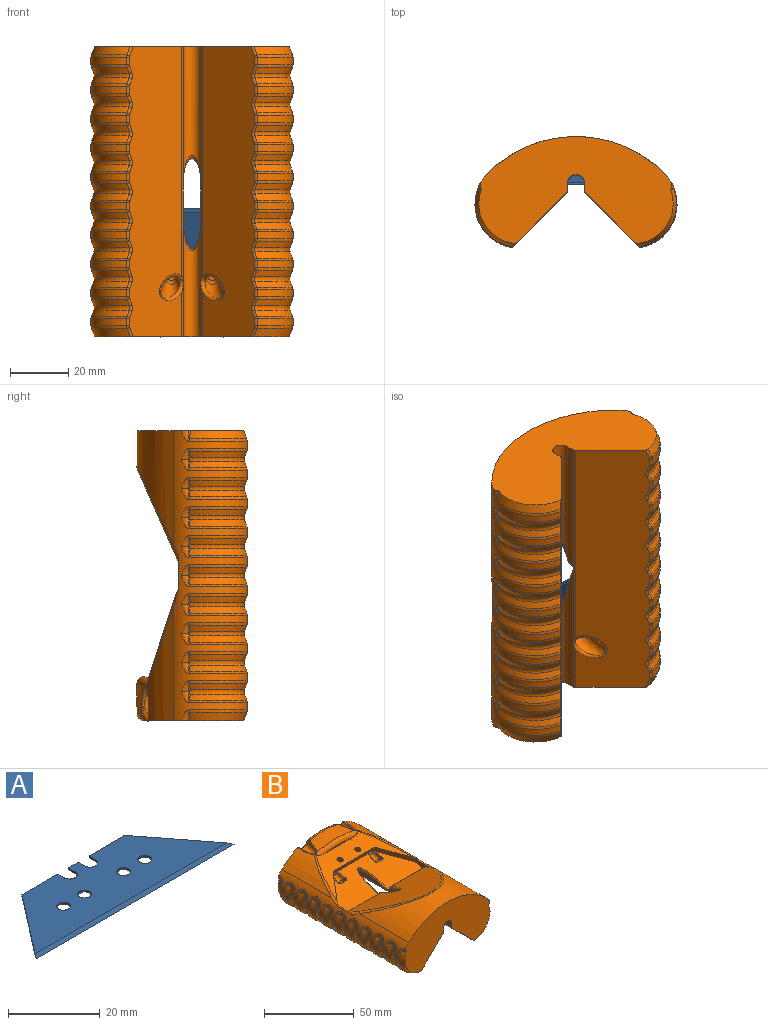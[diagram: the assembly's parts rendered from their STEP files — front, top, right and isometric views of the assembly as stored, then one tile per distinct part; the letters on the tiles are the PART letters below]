
ASSEMBLY  parts=2 mates=1
PART A: 19 faces, bbox 61x19x0.5 mm
  f0: plane 19x14.66mm, normal (-0.79,0.61,0), area 11.6mm2, adj f2,f3,f8,f17,f18
  f1: plane 19x14.66mm, normal (0.79,0.61,0), area 11.6mm2, adj f2,f3,f9,f17,f18
  f2: plane 59.02x17.71mm, normal (0,0,1), area 753.2mm2, adj f0,f1,f4,f5,f6,f7,f8,f9
  f3: plane 59.02x17.71mm, normal (0,0,-1), area 753.2mm2, adj f0,f1,f4,f5,f6,f7,f8,f9
  f4: plane 3.05x0.5mm, normal (0,1,0), area 1.5mm2, adj f2,f3,f5,f12
  f5: plane 2x0.5mm, normal (-1,0,0), area 1mm2, adj f2,f3,f4,f6
  f6: cylinder r=1.65mm len=3.3mm, axis (0,0,-1), area 2.6mm2, adj f2,f3,f5,f7
  f7: plane 2x0.5mm, normal (1,0,0), area 1mm2, adj f2,f3,f6,f8
  f8: plane 11.01x0.5mm, normal (0,1,0), area 5.5mm2, adj f0,f2,f3,f7
  f9: plane 11.01x0.5mm, normal (0,1,0), area 5.5mm2, adj f1,f2,f3,f10
  f10: plane 2x0.5mm, normal (-1,0,0), area 1mm2, adj f2,f3,f9,f11
  f11: cylinder r=1.65mm len=3.3mm, axis (0,0,-1), area 2.6mm2, adj f2,f3,f10,f12
  f12: plane 2x0.5mm, normal (1,0,0), area 1mm2, adj f2,f3,f4,f11
  f13: cylinder r=1.5mm len=3mm, axis (0,0,-1), area 4.7mm2, adj f2,f3
  f14: cylinder r=1.5mm len=3mm, axis (0,0,-1), area 4.7mm2, adj f2,f3
  f15: cylinder r=1.5mm len=3mm, axis (0,0,-1), area 4.7mm2, adj f2,f3
  f16: cylinder r=1.5mm len=3mm, axis (0,0,-1), area 4.7mm2, adj f2,f3
  f17: plane 61x1.29mm, normal (0,-0.19,0.98), area 78.6mm2, adj f0,f1,f2,f18
  f18: plane 61x1.29mm, normal (0,-0.19,-0.98), area 78.6mm2, adj f0,f1,f3,f17
PART B: 395 faces, bbox 78.7x113.5x44.1 mm
  f0: plane 47.73x2.33mm, normal (1,0,0), area 102.8mm2, adj f4,f19,f263,f394
  f1: plane 48.81x2.33mm, normal (-1,0,0), area 112.2mm2, adj f7,f17,f388,f389,f390,f393
  f2: cylinder r=43mm len=39.01mm, axis (0,1,0), area 409.2mm2, adj f4,f5,f94,f155
  f3: cylinder r=43mm len=30.05mm, axis (0,1,0), area 245.3mm2, adj f94,f95,f156,f159,f160,f246
  f4: plane 68.06x36.3mm, normal (0,1,0), area 1526.5mm2, adj f0,f2,f5,f6,f8,f9,f10,f16
  f5: cylinder r=15mm len=100mm, axis (0,1,0), area 1096.3mm2, adj f2,f4,f7,f13,f20,f51,f155,f203
  f6: plane 100x18.06mm, normal (0.71,0,-0.71), area 2413.3mm2, adj f4,f7,f266,f267,f268,f269,f270,f271
  f7: plane 67.06x36.92mm, normal (0,-1,0), area 1601.5mm2, adj f1,f5,f6,f8,f9,f15,f17,f20
  f8: cylinder r=15mm len=100mm, axis (0,1,0), area 1092.7mm2, adj f4,f7,f10,f14,f20,f52,f154,f163
  f9: plane 100x18.06mm, normal (-0.71,0,-0.71), area 2413.1mm2, adj f4,f7,f325,f326,f327,f328,f329,f330
  f10: cylinder r=43mm len=39.01mm, axis (0,1,0), area 409.2mm2, adj f4,f8,f95,f154
  f11: plane 32.7x3.41mm, normal (0,-0.95,-0.31), area 91.9mm2, adj f12,f13,f14,f25,f28,f31,f250,f255
  f12: plane 62x24.87mm, normal (0,-0.31,0.95), area 1116.5mm2, adj f11,f13,f14,f21,f22,f23,f24,f250
  f13: plane 20.34x15.87mm, normal (0.79,-0.58,-0.19), area 72.5mm2, adj f5,f11,f12,f21,f25,f51,f155,f255
  f14: plane 20.34x15.87mm, normal (-0.79,-0.58,-0.19), area 72.5mm2, adj f8,f11,f12,f22,f25,f52,f154,f257
  f15: plane 48.81x2.33mm, normal (1,0,0), area 112.2mm2, adj f7,f17,f384,f385,f386,f394
  f16: plane 47.73x2.33mm, normal (-1,0,0), area 102.8mm2, adj f4,f19,f265,f393
  f17: cylinder r=3mm len=46.59mm, axis (0,1,0), area 384.1mm2, adj f1,f7,f15,f387
  f18: plane 62x34.72mm, normal (0,0.41,0.91), area 1609.9mm2, adj f21,f22,f243,f244,f245,f247,f248,f386
  f19: cylinder r=3mm len=40.56mm, axis (0,1,0), area 316.9mm2, adj f0,f4,f16,f264
  f20: cylinder r=43mm len=60.81mm, axis (0,1,0), area 1458.6mm2, adj f5,f7,f8,f244
  f21: plane 10.53x3.88mm, normal (1,0,0), area 22.4mm2, adj f12,f13,f18,f24,f51,f245,f247
  f22: plane 10.53x3.88mm, normal (-1,0,0), area 22.4mm2, adj f12,f14,f18,f23,f52,f243,f248
  f23: plane 26.92x1.51mm, normal (0,0.95,0.31), area 42.8mm2, adj f12,f22,f248,f390
  f24: plane 26.92x1.51mm, normal (0,0.95,0.31), area 42.8mm2, adj f12,f21,f247,f384
  f25: plane 60.18x30.27mm, normal (0,-0.31,0.95), area 633.1mm2, adj f11,f13,f14,f26,f43,f44,f154,f155
  f26: plane 16.93x0.89mm, normal (0,-0.95,-0.31), area 10.6mm2, adj f25,f246
  f27: plane 3.53x3.35mm, normal (0,-0.95,-0.31), area 1.7mm2, adj f28,f40
  f28: cone r=1.85mm half-angle=1deg, axis (0,-0.95,-0.31), area 56.8mm2, adj f11,f27,f29
  f29: cone r=1.85mm half-angle=6deg, axis (0,-0.95,-0.31), area 35.6mm2, adj f28,f30,f256,f257,f259,f262
  f30: plane 3.94x1.02mm, normal (0,0.95,0.31), area 1mm2, adj f29,f41,f256,f259
  f31: cone r=1.85mm half-angle=1deg, axis (0,-0.95,-0.31), area 56.8mm2, adj f11,f32,f34
  f32: plane 3.53x3.35mm, normal (0,-0.95,-0.31), area 1.7mm2, adj f31,f39
  f33: plane 3.94x1.02mm, normal (0,0.95,0.31), area 1mm2, adj f34,f42,f249,f252
  f34: cone r=1.85mm half-angle=6deg, axis (0,-0.95,-0.31), area 35.6mm2, adj f31,f33,f249,f250,f252,f255
  f35: cylinder r=3mm len=14.23mm, axis (0,0.95,0.31), area 166.3mm2, adj f4,f36,f95,f162
  f36: plane 6x5.71mm, normal (0,0.95,0.31), area 20.2mm2, adj f35,f40
  f37: cylinder r=3mm len=14.23mm, axis (0,0.95,0.31), area 166.2mm2, adj f4,f38,f94,f157
  f38: plane 6x5.71mm, normal (0,0.95,0.31), area 20.2mm2, adj f37,f39
  f39: cylinder r=1.6mm len=8.6mm, axis (0,0.95,0.31), area 80.4mm2, adj f32,f38
  f40: cylinder r=1.6mm len=8.6mm, axis (0,0.95,0.31), area 80.4mm2, adj f27,f36
  f41: plane 3.93x2.95mm, normal (0,0.45,0.89), area 11.5mm2, adj f30,f256,f259,f260
  f42: plane 3.93x2.95mm, normal (0,0.45,0.89), area 11.5mm2, adj f33,f249,f252,f253
  f43: cylinder r=1.75mm len=4.89mm, axis (0,-0.31,0.95), area 44mm2, adj f25,f48
  f44: cylinder r=1.75mm len=4.89mm, axis (0,-0.31,0.95), area 44mm2, adj f25,f46
  f45: cone r=2mm half-angle=8deg, axis (0,0.31,-0.95), area 138.5mm2, adj f47,f392
  f46: plane 3.86x3.67mm, normal (0,0.31,-0.95), area 2.1mm2, adj f44,f47
  f47: cone r=2mm half-angle=1deg, axis (0,0.31,-0.95), area 49.4mm2, adj f45,f46
  f48: plane 3.86x3.67mm, normal (0,0.31,-0.95), area 2.1mm2, adj f43,f49
  f49: cone r=2mm half-angle=1deg, axis (0,0.31,-0.95), area 49.4mm2, adj f48,f50
  f50: cone r=2mm half-angle=8deg, axis (0,0.31,-0.95), area 138.5mm2, adj f49,f391
  f51: cylinder r=0.54mm len=13.4mm, axis (0,1,0), area 14.9mm2, adj f5,f13,f21,f245
  f52: cylinder r=0.54mm len=13.4mm, axis (0,1,0), area 14.9mm2, adj f8,f14,f22,f243
  f53: cone r=13.67mm half-angle=22deg, axis (0,-1,0), area 78.6mm2, adj f4,f116,f201,f383
  f54: cone r=15mm half-angle=22deg, axis (0,1,0), area 58.4mm2, adj f118,f144,f197,f379
  f55: cone r=13.67mm half-angle=22deg, axis (0,-1,0), area 58.4mm2, adj f117,f144,f198,f377
  f56: cone r=15mm half-angle=22deg, axis (0,1,0), area 58.4mm2, adj f120,f143,f193,f373
  f57: cone r=13.67mm half-angle=22deg, axis (0,-1,0), area 58.4mm2, adj f119,f143,f194,f371
  f58: cone r=15mm half-angle=22deg, axis (0,1,0), area 58.4mm2, adj f122,f142,f189,f367
  f59: cone r=13.67mm half-angle=22deg, axis (0,-1,0), area 58.4mm2, adj f121,f142,f190,f365
  f60: cone r=15mm half-angle=22deg, axis (0,1,0), area 58.4mm2, adj f124,f141,f185,f361
  f61: cone r=13.67mm half-angle=22deg, axis (0,-1,0), area 58.4mm2, adj f123,f141,f186,f359
  f62: cone r=15mm half-angle=22deg, axis (0,1,0), area 58.4mm2, adj f126,f140,f181,f355
  f63: cone r=13.67mm half-angle=22deg, axis (0,-1,0), area 58.4mm2, adj f125,f140,f182,f353
  f64: cone r=15mm half-angle=22deg, axis (0,1,0), area 58.4mm2, adj f128,f139,f177,f349
  f65: cone r=13.67mm half-angle=22deg, axis (0,-1,0), area 58.4mm2, adj f127,f139,f178,f347
  f66: cone r=15mm half-angle=22deg, axis (0,1,0), area 58.4mm2, adj f130,f138,f173,f343
  f67: cone r=13.67mm half-angle=22deg, axis (0,-1,0), area 58.4mm2, adj f129,f138,f174,f341
  f68: cone r=15mm half-angle=22deg, axis (0,1,0), area 58.4mm2, adj f132,f137,f169,f337
  f69: cone r=13.67mm half-angle=22deg, axis (0,-1,0), area 58.4mm2, adj f131,f137,f170,f335
  f70: cone r=15mm half-angle=22deg, axis (0,1,0), area 58.4mm2, adj f134,f136,f165,f331
  f71: cone r=13.67mm half-angle=22deg, axis (0,-1,0), area 58.4mm2, adj f133,f136,f166,f329
  f72: cone r=15mm half-angle=22deg, axis (0,1,0), area 78.6mm2, adj f7,f135,f163,f325
  f73: cone r=13.67mm half-angle=22deg, axis (0,1,0), area 78.4mm2, adj f7,f96,f241,f266
  f74: cone r=15mm half-angle=22deg, axis (0,-1,0), area 58.2mm2, adj f98,f153,f237,f270
  f75: cone r=13.67mm half-angle=22deg, axis (0,1,0), area 58.2mm2, adj f97,f153,f238,f272
  f76: cone r=15mm half-angle=22deg, axis (0,-1,0), area 58.2mm2, adj f100,f152,f233,f276
  f77: cone r=13.67mm half-angle=22deg, axis (0,1,0), area 58.2mm2, adj f99,f152,f234,f278
  f78: cone r=15mm half-angle=22deg, axis (0,-1,0), area 58.2mm2, adj f102,f151,f229,f282
  f79: cone r=13.67mm half-angle=22deg, axis (0,1,0), area 58.2mm2, adj f101,f151,f230,f284
  f80: cone r=15mm half-angle=22deg, axis (0,-1,0), area 58.2mm2, adj f104,f150,f225,f288
  f81: cone r=13.67mm half-angle=22deg, axis (0,1,0), area 58.2mm2, adj f103,f150,f226,f290
  f82: cone r=15mm half-angle=22deg, axis (0,-1,0), area 58.2mm2, adj f106,f149,f221,f294
  f83: cone r=13.67mm half-angle=22deg, axis (0,1,0), area 58.2mm2, adj f105,f149,f222,f296
  f84: cone r=15mm half-angle=22deg, axis (0,-1,0), area 58.2mm2, adj f108,f148,f217,f300
  f85: cone r=13.67mm half-angle=22deg, axis (0,1,0), area 58.2mm2, adj f107,f148,f218,f302
  f86: cone r=15mm half-angle=22deg, axis (0,-1,0), area 58.2mm2, adj f110,f147,f213,f306
  f87: cone r=13.67mm half-angle=22deg, axis (0,1,0), area 58.2mm2, adj f109,f147,f214,f308
  f88: cone r=15mm half-angle=22deg, axis (0,-1,0), area 58.2mm2, adj f112,f146,f209,f312
  f89: cone r=13.67mm half-angle=22deg, axis (0,1,0), area 58.2mm2, adj f111,f146,f210,f314
  f90: cone r=15mm half-angle=22deg, axis (0,-1,0), area 58.2mm2, adj f114,f145,f205,f318
  f91: cone r=13.67mm half-angle=22deg, axis (0,1,0), area 58.2mm2, adj f113,f145,f206,f320
  f92: cone r=15mm half-angle=22deg, axis (0,-1,0), area 78.4mm2, adj f4,f115,f203,f324
  f93: cone r=41.38mm half-angle=45deg, axis (0,-1,0), area 24.5mm2, adj f4,f157,f159,f162
  f94: bspline ~12.8x6.53mm, area 25.4mm2, adj f2,f3,f4,f37,f155,f156,f246
  f95: bspline ~13.98x6.44mm, area 25.4mm2, adj f3,f4,f10,f35,f154,f160,f246
  f96: bspline ~20.96x8.4mm, area 1.2mm2, adj f7,f73,f242
  f97: bspline ~20.96x8.4mm, area 1.4mm2, adj f75,f98,f153,f240
  f98: bspline ~21.58x8.63mm, area 1.4mm2, adj f74,f97,f153,f239
  f99: bspline ~20.96x8.4mm, area 1.4mm2, adj f77,f100,f152,f236
  f100: bspline ~21.58x8.63mm, area 1.4mm2, adj f76,f99,f152,f235
  f101: bspline ~20.96x8.4mm, area 1.4mm2, adj f79,f102,f151,f232
  f102: bspline ~21.58x8.63mm, area 1.4mm2, adj f78,f101,f151,f231
  f103: bspline ~20.96x8.4mm, area 1.4mm2, adj f81,f104,f150,f228
  f104: bspline ~21.58x8.63mm, area 1.4mm2, adj f80,f103,f150,f227
  f105: bspline ~20.96x8.4mm, area 1.4mm2, adj f83,f106,f149,f224
  f106: bspline ~21.58x8.63mm, area 1.4mm2, adj f82,f105,f149,f223
  f107: bspline ~20.96x8.4mm, area 1.4mm2, adj f85,f108,f148,f220
  f108: bspline ~21.58x8.63mm, area 1.4mm2, adj f84,f107,f148,f219
  f109: bspline ~20.96x8.4mm, area 1.4mm2, adj f87,f110,f147,f216
  f110: bspline ~21.58x8.63mm, area 1.4mm2, adj f86,f109,f147,f215
  f111: bspline ~20.96x8.4mm, area 1.4mm2, adj f89,f112,f146,f212
  f112: bspline ~21.58x8.63mm, area 1.4mm2, adj f88,f111,f146,f211
  f113: bspline ~20.96x8.4mm, area 1.4mm2, adj f91,f114,f145,f208
  f114: bspline ~21.58x8.63mm, area 1.4mm2, adj f90,f113,f145,f207
  f115: bspline ~21.58x8.63mm, area 1.2mm2, adj f4,f92,f204
  f116: bspline ~20.96x8.4mm, area 1.2mm2, adj f4,f53,f202
  f117: bspline ~20.96x8.4mm, area 1.4mm2, adj f55,f118,f144,f200
  f118: bspline ~21.57x8.63mm, area 1.4mm2, adj f54,f117,f144,f199
  f119: bspline ~20.96x8.4mm, area 1.4mm2, adj f57,f120,f143,f196
  f120: bspline ~21.57x8.63mm, area 1.4mm2, adj f56,f119,f143,f195
  f121: bspline ~20.96x8.4mm, area 1.4mm2, adj f59,f122,f142,f192
  f122: bspline ~21.57x8.63mm, area 1.4mm2, adj f58,f121,f142,f191
  f123: bspline ~20.96x8.4mm, area 1.4mm2, adj f61,f124,f141,f188
  f124: bspline ~21.57x8.63mm, area 1.4mm2, adj f60,f123,f141,f187
  f125: bspline ~20.96x8.4mm, area 1.4mm2, adj f63,f126,f140,f184
  f126: bspline ~21.57x8.63mm, area 1.4mm2, adj f62,f125,f140,f183
  f127: bspline ~20.96x8.4mm, area 1.4mm2, adj f65,f128,f139,f180
  f128: bspline ~21.57x8.63mm, area 1.4mm2, adj f64,f127,f139,f179
  f129: bspline ~20.96x8.4mm, area 1.4mm2, adj f67,f130,f138,f176
  f130: bspline ~21.57x8.63mm, area 1.4mm2, adj f66,f129,f138,f175
  f131: bspline ~20.96x8.4mm, area 1.4mm2, adj f69,f132,f137,f172
  f132: bspline ~21.57x8.63mm, area 1.4mm2, adj f68,f131,f137,f171
  f133: bspline ~20.96x8.4mm, area 1.4mm2, adj f71,f134,f136,f168
  f134: bspline ~21.57x8.63mm, area 1.4mm2, adj f70,f133,f136,f167
  f135: bspline ~21.57x8.63mm, area 1.2mm2, adj f7,f72,f164
  f136: torus R=15.82mm, axis (0,1,0), area 38.6mm2, adj f70,f71,f133,f134,f330
  f137: torus R=15.82mm, axis (0,1,0), area 38.6mm2, adj f68,f69,f131,f132,f336
  f138: torus R=15.82mm, axis (0,1,0), area 38.6mm2, adj f66,f67,f129,f130,f342
  f139: torus R=15.82mm, axis (0,1,0), area 38.6mm2, adj f64,f65,f127,f128,f348
  f140: torus R=15.82mm, axis (0,1,0), area 38.6mm2, adj f62,f63,f125,f126,f354
  f141: torus R=15.82mm, axis (0,1,0), area 38.6mm2, adj f60,f61,f123,f124,f360
  f142: torus R=15.82mm, axis (0,1,0), area 38.6mm2, adj f58,f59,f121,f122,f366
  f143: torus R=15.82mm, axis (0,1,0), area 38.6mm2, adj f56,f57,f119,f120,f372
  f144: torus R=15.82mm, axis (0,1,0), area 38.6mm2, adj f54,f55,f117,f118,f378
  f145: torus R=15.82mm, axis (0,-1,0), area 38.6mm2, adj f90,f91,f113,f114,f319
  f146: torus R=15.82mm, axis (0,-1,0), area 38.6mm2, adj f88,f89,f111,f112,f313
  f147: torus R=15.82mm, axis (0,-1,0), area 38.6mm2, adj f86,f87,f109,f110,f307
  f148: torus R=15.82mm, axis (0,-1,0), area 38.6mm2, adj f84,f85,f107,f108,f301
  f149: torus R=15.82mm, axis (0,-1,0), area 38.6mm2, adj f82,f83,f105,f106,f295
  f150: torus R=15.82mm, axis (0,-1,0), area 38.6mm2, adj f80,f81,f103,f104,f289
  f151: torus R=15.82mm, axis (0,-1,0), area 38.6mm2, adj f78,f79,f101,f102,f283
  f152: torus R=15.82mm, axis (0,-1,0), area 38.6mm2, adj f76,f77,f99,f100,f277
  f153: torus R=15.82mm, axis (0,-1,0), area 38.6mm2, adj f74,f75,f97,f98,f271
  f154: bspline ~33.76x16.49mm, area 50.3mm2, adj f8,f10,f14,f25,f95,f246
  f155: bspline ~33.76x16.49mm, area 50.3mm2, adj f2,f5,f13,f25,f94,f246
  f156: bspline ~3.1x2.09mm, area 2.2mm2, adj f3,f94,f157,f158
  f157: bspline ~7.53x6.81mm, area 12.4mm2, adj f4,f37,f93,f156,f158
  f158: bspline ~2.18x2.11mm, area 0.5mm2, adj f156,f157,f159
  f159: torus R=40.6mm, axis (0,1,0), area 38.4mm2, adj f3,f93,f158,f161
  f160: bspline ~3.1x2.09mm, area 2.2mm2, adj f3,f95,f161,f162
  f161: bspline ~2.18x2.11mm, area 0.5mm2, adj f159,f160,f162
  f162: bspline ~7.48x6.88mm, area 12.4mm2, adj f4,f35,f93,f160,f161
  f163: torus R=12.6mm, axis (0,-1,0), area 24.1mm2, adj f8,f72,f164,f326
  f164: bspline ~4.93x2.94mm, area 6.9mm2, adj f7,f8,f135,f163
  f165: torus R=12.6mm, axis (0,-1,0), area 24.1mm2, adj f8,f70,f167,f332
  f166: torus R=12.6mm, axis (0,-1,0), area 24.1mm2, adj f8,f71,f168,f328
  f167: bspline ~4.93x2.94mm, area 6.9mm2, adj f8,f134,f165,f168
  f168: bspline ~4.93x3.12mm, area 6.9mm2, adj f8,f133,f166,f167
  f169: torus R=12.6mm, axis (0,-1,0), area 24.1mm2, adj f8,f68,f171,f338
  f170: torus R=12.6mm, axis (0,-1,0), area 24.1mm2, adj f8,f69,f172,f334
  f171: bspline ~4.93x2.94mm, area 6.9mm2, adj f8,f132,f169,f172
  f172: bspline ~4.93x2.92mm, area 6.9mm2, adj f8,f131,f170,f171
  f173: torus R=12.6mm, axis (0,-1,0), area 24.1mm2, adj f8,f66,f175,f344
  f174: torus R=12.6mm, axis (0,-1,0), area 24.1mm2, adj f8,f67,f176,f340
  f175: bspline ~4.93x2.94mm, area 6.9mm2, adj f8,f130,f173,f176
  f176: bspline ~4.93x3.12mm, area 6.9mm2, adj f8,f129,f174,f175
  f177: torus R=12.6mm, axis (0,-1,0), area 24.1mm2, adj f8,f64,f179,f350
  f178: torus R=12.6mm, axis (0,-1,0), area 24.1mm2, adj f8,f65,f180,f346
  f179: bspline ~4.93x2.94mm, area 6.9mm2, adj f8,f128,f177,f180
  f180: bspline ~4.93x3.12mm, area 6.9mm2, adj f8,f127,f178,f179
  f181: torus R=12.6mm, axis (0,-1,0), area 24.1mm2, adj f8,f62,f183,f356
  f182: torus R=12.6mm, axis (0,-1,0), area 24.1mm2, adj f8,f63,f184,f352
  f183: bspline ~4.93x2.94mm, area 6.9mm2, adj f8,f126,f181,f184
  f184: bspline ~4.93x3.12mm, area 6.9mm2, adj f8,f125,f182,f183
  f185: torus R=12.6mm, axis (0,-1,0), area 24.1mm2, adj f8,f60,f187,f362
  f186: torus R=12.6mm, axis (0,-1,0), area 24.1mm2, adj f8,f61,f188,f358
  f187: bspline ~4.93x2.94mm, area 6.9mm2, adj f8,f124,f185,f188
  f188: bspline ~4.93x3.12mm, area 6.9mm2, adj f8,f123,f186,f187
  f189: torus R=12.6mm, axis (0,-1,0), area 24.1mm2, adj f8,f58,f191,f368
  f190: torus R=12.6mm, axis (0,-1,0), area 24.1mm2, adj f8,f59,f192,f364
  f191: bspline ~4.93x2.94mm, area 6.9mm2, adj f8,f122,f189,f192
  f192: bspline ~4.93x3.12mm, area 6.9mm2, adj f8,f121,f190,f191
  f193: torus R=12.6mm, axis (0,-1,0), area 24.1mm2, adj f8,f56,f195,f374
  f194: torus R=12.6mm, axis (0,-1,0), area 24.1mm2, adj f8,f57,f196,f370
  f195: bspline ~4.93x2.94mm, area 6.9mm2, adj f8,f120,f193,f196
  f196: bspline ~4.93x3.12mm, area 6.9mm2, adj f8,f119,f194,f195
  f197: torus R=12.6mm, axis (0,-1,0), area 24.1mm2, adj f8,f54,f199,f380
  f198: torus R=12.6mm, axis (0,-1,0), area 24.1mm2, adj f8,f55,f200,f376
  f199: bspline ~4.93x2.94mm, area 6.9mm2, adj f8,f118,f197,f200
  f200: bspline ~4.93x3.12mm, area 6.9mm2, adj f8,f117,f198,f199
  f201: torus R=12.6mm, axis (0,-1,0), area 24.1mm2, adj f8,f53,f202,f382
  f202: bspline ~4.93x2.94mm, area 6.9mm2, adj f4,f8,f116,f201
  f203: torus R=12.6mm, axis (0,1,0), area 24.1mm2, adj f5,f92,f204,f323
  f204: bspline ~4.93x2.94mm, area 6.9mm2, adj f4,f5,f115,f203
  f205: torus R=12.6mm, axis (0,1,0), area 24.1mm2, adj f5,f90,f207,f317
  f206: torus R=12.6mm, axis (0,1,0), area 24.1mm2, adj f5,f91,f208,f321
  f207: bspline ~4.93x2.94mm, area 6.9mm2, adj f5,f114,f205,f208
  f208: bspline ~4.93x3.12mm, area 6.9mm2, adj f5,f113,f206,f207
  f209: torus R=12.6mm, axis (0,1,0), area 24.1mm2, adj f5,f88,f211,f311
  f210: torus R=12.6mm, axis (0,1,0), area 24.1mm2, adj f5,f89,f212,f315
  f211: bspline ~4.93x2.94mm, area 6.9mm2, adj f5,f112,f209,f212
  f212: bspline ~4.93x2.92mm, area 6.9mm2, adj f5,f111,f210,f211
  f213: torus R=12.6mm, axis (0,1,0), area 24.1mm2, adj f5,f86,f215,f305
  f214: torus R=12.6mm, axis (0,1,0), area 24.1mm2, adj f5,f87,f216,f309
  f215: bspline ~4.93x2.94mm, area 6.9mm2, adj f5,f110,f213,f216
  f216: bspline ~4.93x3.12mm, area 6.9mm2, adj f5,f109,f214,f215
  f217: torus R=12.6mm, axis (0,1,0), area 24.1mm2, adj f5,f84,f219,f299
  f218: torus R=12.6mm, axis (0,1,0), area 24.1mm2, adj f5,f85,f220,f303
  f219: bspline ~4.93x2.94mm, area 6.9mm2, adj f5,f108,f217,f220
  f220: bspline ~4.93x3.12mm, area 6.9mm2, adj f5,f107,f218,f219
  f221: torus R=12.6mm, axis (0,1,0), area 24.1mm2, adj f5,f82,f223,f293
  f222: torus R=12.6mm, axis (0,1,0), area 24.1mm2, adj f5,f83,f224,f297
  f223: bspline ~4.93x2.94mm, area 6.9mm2, adj f5,f106,f221,f224
  f224: bspline ~4.93x3.12mm, area 6.9mm2, adj f5,f105,f222,f223
  f225: torus R=12.6mm, axis (0,1,0), area 24.1mm2, adj f5,f80,f227,f287
  f226: torus R=12.6mm, axis (0,1,0), area 24.1mm2, adj f5,f81,f228,f291
  f227: bspline ~4.93x2.94mm, area 6.9mm2, adj f5,f104,f225,f228
  f228: bspline ~4.93x3.12mm, area 6.9mm2, adj f5,f103,f226,f227
  f229: torus R=12.6mm, axis (0,1,0), area 24.1mm2, adj f5,f78,f231,f281
  f230: torus R=12.6mm, axis (0,1,0), area 24.1mm2, adj f5,f79,f232,f285
  f231: bspline ~4.93x2.94mm, area 6.9mm2, adj f5,f102,f229,f232
  f232: bspline ~4.93x3.12mm, area 6.9mm2, adj f5,f101,f230,f231
  f233: torus R=12.6mm, axis (0,1,0), area 24.1mm2, adj f5,f76,f235,f275
  f234: torus R=12.6mm, axis (0,1,0), area 24.1mm2, adj f5,f77,f236,f279
  f235: bspline ~4.93x2.94mm, area 6.9mm2, adj f5,f100,f233,f236
  f236: bspline ~4.93x3.12mm, area 6.9mm2, adj f5,f99,f234,f235
  f237: torus R=12.6mm, axis (0,1,0), area 24.1mm2, adj f5,f74,f239,f269
  f238: torus R=12.6mm, axis (0,1,0), area 24.1mm2, adj f5,f75,f240,f273
  f239: bspline ~4.93x2.94mm, area 6.9mm2, adj f5,f98,f237,f240
  f240: bspline ~4.93x3.12mm, area 6.9mm2, adj f5,f97,f238,f239
  f241: torus R=12.6mm, axis (0,1,0), area 24.1mm2, adj f5,f73,f242,f267
  f242: bspline ~4.93x2.94mm, area 6.9mm2, adj f5,f7,f96,f241
  f243: bspline ~8.03x4.43mm, area 13.5mm2, adj f8,f18,f22,f52,f244
  f244: bspline ~60.81x27.67mm, area 130.6mm2, adj f18,f20,f243,f245
  f245: bspline ~8.03x4.43mm, area 13.5mm2, adj f5,f18,f21,f51,f244
  f246: bspline ~47.17x9.47mm, area 130.3mm2, adj f3,f25,f26,f94,f95,f154,f155
  f247: cylinder r=2.4mm len=26.92mm, axis (-1,0,0), area 54.1mm2, adj f18,f21,f24,f385
  f248: cylinder r=2.4mm len=26.92mm, axis (-1,0,0), area 54.1mm2, adj f18,f22,f23,f389
  f249: bspline ~4.08x2.6mm, area 2.3mm2, adj f33,f34,f42,f251
  f250: bspline ~30.37x10.35mm, area 5.3mm2, adj f11,f12,f34,f251
  f251: bspline ~1.96x1.36mm, area 1.2mm2, adj f12,f249,f250,f253
  f252: bspline ~4.08x2.6mm, area 2.3mm2, adj f33,f34,f42,f254
  f253: cylinder r=0.54mm len=3.73mm, axis (-1,0,0), area 1.6mm2, adj f12,f42,f251,f254
  f254: bspline ~1.79x1.35mm, area 1.2mm2, adj f12,f252,f253,f255
  f255: bspline ~29.89x10.19mm, area 5.1mm2, adj f11,f12,f13,f34,f254
  f256: bspline ~4.08x2.6mm, area 2.3mm2, adj f29,f30,f41,f258
  f257: bspline ~29.89x10.19mm, area 5.1mm2, adj f11,f12,f14,f29,f258
  f258: bspline ~1.96x1.36mm, area 1.2mm2, adj f12,f256,f257,f260
  f259: bspline ~4.08x2.6mm, area 2.3mm2, adj f29,f30,f41,f261
  f260: cylinder r=0.54mm len=3.73mm, axis (-1,0,0), area 1.6mm2, adj f12,f41,f258,f261
  f261: bspline ~1.79x1.35mm, area 1.2mm2, adj f12,f259,f260,f262
  f262: bspline ~30.37x10.35mm, area 5.3mm2, adj f11,f12,f29,f261
  f263: cylinder r=0.54mm len=10.03mm, axis (0,-0.95,-0.31), area 8.2mm2, adj f0,f12,f264,f384,f394
  f264: bspline ~11.06x7.08mm, area 27.7mm2, adj f12,f19,f263,f265
  f265: cylinder r=0.54mm len=10.03mm, axis (0,0.95,0.31), area 8.2mm2, adj f12,f16,f264,f390,f393
  f266: bspline ~9.17x4.1mm, area 3.7mm2, adj f6,f7,f73,f267
  f267: bspline ~1.83x1.16mm, area 0.8mm2, adj f6,f241,f266,f268
  f268: cylinder r=1.08mm len=2.47mm, axis (0,1,0), area 2.6mm2, adj f5,f6,f267,f269
  f269: bspline ~1.83x1.16mm, area 0.8mm2, adj f6,f237,f268,f270
  f270: bspline ~8.89x3.99mm, area 2.5mm2, adj f6,f74,f269,f271
  f271: bspline ~3.54x1.39mm, area 2mm2, adj f6,f153,f270,f272
  f272: bspline ~8.89x3.99mm, area 2.5mm2, adj f6,f75,f271,f273
  f273: bspline ~1.83x1.16mm, area 0.8mm2, adj f6,f238,f272,f274
  f274: cylinder r=1.08mm len=2.47mm, axis (0,1,0), area 2.6mm2, adj f5,f6,f273,f275
  f275: bspline ~1.83x1.16mm, area 0.8mm2, adj f6,f233,f274,f276
  f276: bspline ~7.31x3.4mm, area 2.5mm2, adj f6,f76,f275,f277
  f277: bspline ~3.54x1.39mm, area 2mm2, adj f6,f152,f276,f278
  f278: bspline ~8.89x3.99mm, area 2.5mm2, adj f6,f77,f277,f279
  f279: bspline ~1.83x1.16mm, area 0.8mm2, adj f6,f234,f278,f280
  f280: cylinder r=1.08mm len=2.47mm, axis (0,1,0), area 2.6mm2, adj f5,f6,f279,f281
  f281: bspline ~1.83x1.16mm, area 0.8mm2, adj f6,f229,f280,f282
  f282: bspline ~8.89x3.99mm, area 2.5mm2, adj f6,f78,f281,f283
  f283: bspline ~3.54x1.39mm, area 2mm2, adj f6,f151,f282,f284
  f284: bspline ~8.89x3.99mm, area 2.5mm2, adj f6,f79,f283,f285
  f285: bspline ~1.83x1.16mm, area 0.8mm2, adj f6,f230,f284,f286
  f286: cylinder r=1.08mm len=2.47mm, axis (0,1,0), area 2.6mm2, adj f5,f6,f285,f287
  f287: bspline ~1.83x1.16mm, area 0.8mm2, adj f6,f225,f286,f288
  f288: bspline ~7.31x3.4mm, area 2.5mm2, adj f6,f80,f287,f289
  f289: bspline ~3.54x1.39mm, area 2mm2, adj f6,f150,f288,f290
  f290: bspline ~8.89x3.99mm, area 2.5mm2, adj f6,f81,f289,f291
  f291: bspline ~1.83x1.16mm, area 0.8mm2, adj f6,f226,f290,f292
  f292: cylinder r=1.08mm len=2.47mm, axis (0,1,0), area 2.6mm2, adj f5,f6,f291,f293
  f293: bspline ~1.83x1.16mm, area 0.8mm2, adj f6,f221,f292,f294
  f294: bspline ~7.31x3.4mm, area 2.5mm2, adj f6,f82,f293,f295
  f295: bspline ~3.54x1.39mm, area 2mm2, adj f6,f149,f294,f296
  f296: bspline ~8.89x3.99mm, area 2.5mm2, adj f6,f83,f295,f297
  f297: bspline ~1.83x1.16mm, area 0.8mm2, adj f6,f222,f296,f298
  f298: cylinder r=1.08mm len=2.47mm, axis (0,1,0), area 2.6mm2, adj f5,f6,f297,f299
  f299: bspline ~1.83x1.16mm, area 0.8mm2, adj f6,f217,f298,f300
  f300: bspline ~7.31x3.4mm, area 2.5mm2, adj f6,f84,f299,f301
  f301: bspline ~3.54x1.39mm, area 2mm2, adj f6,f148,f300,f302
  f302: bspline ~8.89x3.99mm, area 2.5mm2, adj f6,f85,f301,f303
  f303: bspline ~1.83x1.16mm, area 0.8mm2, adj f6,f218,f302,f304
  f304: cylinder r=1.08mm len=2.47mm, axis (0,1,0), area 2.6mm2, adj f5,f6,f303,f305
  f305: bspline ~1.83x1.16mm, area 0.8mm2, adj f6,f213,f304,f306
  f306: bspline ~7.31x3.4mm, area 2.5mm2, adj f6,f86,f305,f307
  f307: bspline ~3.54x1.39mm, area 2mm2, adj f6,f147,f306,f308
  f308: bspline ~8.89x3.99mm, area 2.5mm2, adj f6,f87,f307,f309
  f309: bspline ~1.83x1.16mm, area 0.8mm2, adj f6,f214,f308,f310
  f310: cylinder r=1.08mm len=2.47mm, axis (0,1,0), area 2.6mm2, adj f5,f6,f309,f311
  f311: bspline ~1.83x1.16mm, area 0.8mm2, adj f6,f209,f310,f312
  f312: bspline ~7.31x3.4mm, area 2.5mm2, adj f6,f88,f311,f313
  f313: bspline ~3.54x1.39mm, area 2mm2, adj f6,f146,f312,f314
  f314: bspline ~8.89x3.99mm, area 2.5mm2, adj f6,f89,f313,f315
  f315: bspline ~1.83x1.16mm, area 0.8mm2, adj f6,f210,f314,f316
  f316: cylinder r=1.08mm len=2.47mm, axis (0,1,0), area 2.6mm2, adj f5,f6,f315,f317
  f317: bspline ~1.83x1.16mm, area 0.8mm2, adj f6,f205,f316,f318
  f318: bspline ~7.31x3.4mm, area 2.5mm2, adj f6,f90,f317,f319
  f319: bspline ~3.54x1.39mm, area 2mm2, adj f6,f145,f318,f320
  f320: bspline ~8.89x3.99mm, area 2.5mm2, adj f6,f91,f319,f321
  f321: bspline ~1.83x1.16mm, area 0.8mm2, adj f6,f206,f320,f322
  f322: cylinder r=1.08mm len=2.47mm, axis (0,1,0), area 2.6mm2, adj f5,f6,f321,f323
  f323: bspline ~1.83x1.16mm, area 0.8mm2, adj f6,f203,f322,f324
  f324: bspline ~9.17x4.1mm, area 3.7mm2, adj f4,f6,f92,f323
  f325: bspline ~9.17x4.1mm, area 3.7mm2, adj f7,f9,f72,f326
  f326: bspline ~1.48x1.16mm, area 0.8mm2, adj f9,f163,f325,f327
  f327: cylinder r=1.08mm len=2.46mm, axis (0,1,0), area 2.6mm2, adj f8,f9,f326,f328
  f328: bspline ~1.49x1.06mm, area 0.8mm2, adj f9,f166,f327,f329
  f329: bspline ~8.91x4mm, area 2.5mm2, adj f9,f71,f328,f330
  f330: bspline ~3.09x1.39mm, area 2mm2, adj f9,f136,f329,f331
  f331: bspline ~8.91x4mm, area 2.5mm2, adj f9,f70,f330,f332
  f332: bspline ~1.48x1.16mm, area 0.8mm2, adj f9,f165,f331,f333
  f333: cylinder r=1.08mm len=2.46mm, axis (0,1,0), area 2.6mm2, adj f8,f9,f332,f334
  f334: bspline ~1.49x1.06mm, area 0.8mm2, adj f9,f170,f333,f335
  f335: bspline ~8.91x4mm, area 2.5mm2, adj f9,f69,f334,f336
  f336: bspline ~3.09x1.39mm, area 2mm2, adj f9,f137,f335,f337
  f337: bspline ~8.91x4mm, area 2.5mm2, adj f9,f68,f336,f338
  f338: bspline ~1.48x1.16mm, area 0.8mm2, adj f9,f169,f337,f339
  f339: cylinder r=1.08mm len=2.46mm, axis (0,1,0), area 2.6mm2, adj f8,f9,f338,f340
  f340: bspline ~1.49x1.06mm, area 0.8mm2, adj f9,f174,f339,f341
  f341: bspline ~8.91x4mm, area 2.5mm2, adj f9,f67,f340,f342
  f342: bspline ~3.09x1.39mm, area 2mm2, adj f9,f138,f341,f343
  f343: bspline ~8.91x4mm, area 2.5mm2, adj f9,f66,f342,f344
  f344: bspline ~1.48x1.16mm, area 0.8mm2, adj f9,f173,f343,f345
  f345: cylinder r=1.08mm len=2.46mm, axis (0,1,0), area 2.6mm2, adj f8,f9,f344,f346
  f346: bspline ~1.49x1.06mm, area 0.8mm2, adj f9,f178,f345,f347
  f347: bspline ~8.91x4mm, area 2.5mm2, adj f9,f65,f346,f348
  f348: bspline ~3.09x1.39mm, area 2mm2, adj f9,f139,f347,f349
  f349: bspline ~8.91x4mm, area 2.5mm2, adj f9,f64,f348,f350
  f350: bspline ~1.48x1.16mm, area 0.8mm2, adj f9,f177,f349,f351
  f351: cylinder r=1.08mm len=2.46mm, axis (0,1,0), area 2.6mm2, adj f8,f9,f350,f352
  f352: bspline ~1.49x1.06mm, area 0.8mm2, adj f9,f182,f351,f353
  f353: bspline ~8.91x4mm, area 2.5mm2, adj f9,f63,f352,f354
  f354: bspline ~3.09x1.39mm, area 2mm2, adj f9,f140,f353,f355
  f355: bspline ~8.91x4mm, area 2.5mm2, adj f9,f62,f354,f356
  f356: bspline ~1.48x1.16mm, area 0.8mm2, adj f9,f181,f355,f357
  f357: cylinder r=1.08mm len=2.46mm, axis (0,1,0), area 2.6mm2, adj f8,f9,f356,f358
  f358: bspline ~1.49x1.06mm, area 0.8mm2, adj f9,f186,f357,f359
  f359: bspline ~8.91x4mm, area 2.5mm2, adj f9,f61,f358,f360
  f360: bspline ~3.09x1.39mm, area 2mm2, adj f9,f141,f359,f361
  f361: bspline ~8.91x4mm, area 2.5mm2, adj f9,f60,f360,f362
  f362: bspline ~1.48x1.16mm, area 0.8mm2, adj f9,f185,f361,f363
  f363: cylinder r=1.08mm len=2.46mm, axis (0,1,0), area 2.6mm2, adj f8,f9,f362,f364
  f364: bspline ~1.49x1.06mm, area 0.8mm2, adj f9,f190,f363,f365
  f365: bspline ~8.91x4mm, area 2.5mm2, adj f9,f59,f364,f366
  f366: bspline ~3.09x1.39mm, area 2mm2, adj f9,f142,f365,f367
  f367: bspline ~8.91x4mm, area 2.5mm2, adj f9,f58,f366,f368
  f368: bspline ~1.48x1.16mm, area 0.8mm2, adj f9,f189,f367,f369
  f369: cylinder r=1.08mm len=2.46mm, axis (0,1,0), area 2.6mm2, adj f8,f9,f368,f370
  f370: bspline ~1.49x1.06mm, area 0.8mm2, adj f9,f194,f369,f371
  f371: bspline ~8.91x4mm, area 2.5mm2, adj f9,f57,f370,f372
  f372: bspline ~3.09x1.39mm, area 2mm2, adj f9,f143,f371,f373
  f373: bspline ~8.91x4mm, area 2.5mm2, adj f9,f56,f372,f374
  f374: bspline ~1.48x1.16mm, area 0.8mm2, adj f9,f193,f373,f375
  f375: cylinder r=1.08mm len=2.46mm, axis (0,1,0), area 2.6mm2, adj f8,f9,f374,f376
  f376: bspline ~1.49x1.06mm, area 0.8mm2, adj f9,f198,f375,f377
  f377: bspline ~8.91x4mm, area 2.5mm2, adj f9,f55,f376,f378
  f378: bspline ~3.09x1.39mm, area 2mm2, adj f9,f144,f377,f379
  f379: bspline ~8.91x4mm, area 2.5mm2, adj f9,f54,f378,f380
  f380: bspline ~1.48x1.16mm, area 0.8mm2, adj f9,f197,f379,f381
  f381: cylinder r=1.08mm len=2.46mm, axis (0,1,0), area 2.6mm2, adj f8,f9,f380,f382
  f382: bspline ~1.49x1.06mm, area 0.8mm2, adj f9,f201,f381,f383
  f383: bspline ~9.17x4.1mm, area 3.7mm2, adj f4,f9,f53,f382
  f384: cylinder r=1.08mm len=2.06mm, axis (0,-0.31,0.95), area 2.7mm2, adj f12,f15,f24,f263,f385,f394
  f385: torus R=1.32mm, axis (1,0,0), area 2.9mm2, adj f15,f247,f384,f386
  f386: cylinder r=1.08mm len=1.61mm, axis (0,0.91,-0.41), area 2.2mm2, adj f15,f18,f385,f387
  f387: bspline ~11.2x8.16mm, area 47.2mm2, adj f17,f18,f386,f388
  f388: cylinder r=1.08mm len=1.61mm, axis (0,0.91,-0.41), area 2.2mm2, adj f1,f18,f387,f389
  f389: torus R=1.32mm, axis (1,0,0), area 2.9mm2, adj f1,f248,f388,f390
  f390: cylinder r=1.08mm len=2.06mm, axis (0,0.31,-0.95), area 2.7mm2, adj f1,f12,f23,f265,f389,f393
  f391: bspline ~9.38x9.21mm, area 42.1mm2, adj f6,f50,f394
  f392: bspline ~9.38x9.21mm, area 42.1mm2, adj f9,f45,f393
  f393: cylinder r=1.62mm len=100mm, axis (0,1,0), area 123.6mm2, adj f1,f4,f7,f9,f16,f265,f390,f392
  f394: cylinder r=1.62mm len=100mm, axis (0,1,0), area 123.6mm2, adj f0,f4,f6,f7,f15,f263,f384,f391
PLACE A rot(axis=(-1,0,0),72deg) t=(-0.06,-7.19,-55.69)mm
PLACE B rot(axis=(-1,0,0),90deg) t=(0,-6.81,-50)mm
MATE planar B.f12 <-> A.f3  axis (0,0.95,0.31) through (0,-5.89,-60.52)mm
